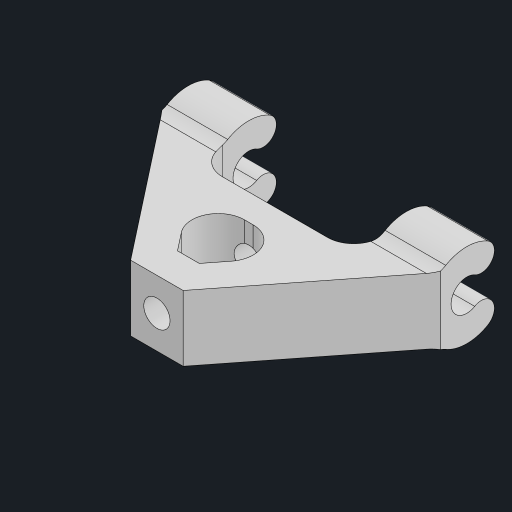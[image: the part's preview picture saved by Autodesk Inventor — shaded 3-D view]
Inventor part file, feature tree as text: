
AUTODESK INVENTOR PART (.ipt)
format: ipt  version: 2023 (Build 270158000, 158)  size: 197,120 bytes
history: native  units: mm
features: sketch x3, extrude x3, other x1, hole x1, mirror x1, fillet x1
ambient origin geometry x8: Origin, YZ Plane, XZ Plane, XY Plane, X Axis, Y Axis, Z Axis, Center Point
bodies: Body1 (feature_tree)
feature tree (10):
  other  "ソリッド1"
  sketch  "スケッチ1"
  extrude  "押し出し1"  Depth=4.0mm
  hole  "穴1"  [1 undecoded]
  sketch  "スケッチ4"
  extrude  "押し出し3"  Depth=13.0mm
  extrude  "押し出し4"  Depth=2.4mm
  mirror  "ミラー1"
  fillet  "フィレット2"  Radius=5.0mm
  sketch  "スケッチ3"
note: 1 required parameter value undecoded (feature->parameter linkage not recoverable at this tier; creation-order binding heuristic only, values carry confidence <= 0.55)
